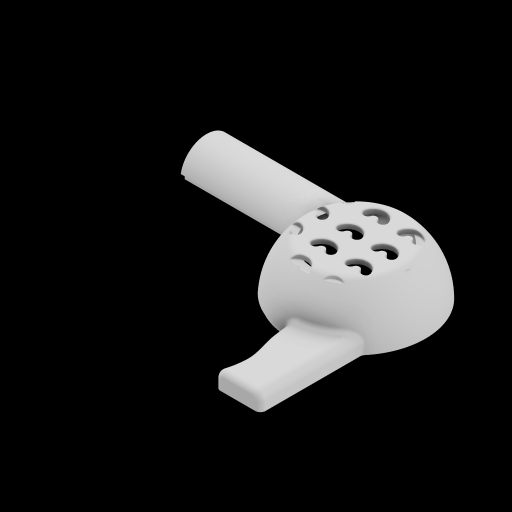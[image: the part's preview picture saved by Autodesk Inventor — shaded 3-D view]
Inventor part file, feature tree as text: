
AUTODESK INVENTOR PART (.ipt)
format: ipt  version: 2024 (Build 280153000, 153)  size: 583,680 bytes
history: native  units: in
note: dims shown in document units (in); Inventor stores cm internally (conversion verified against a paired STEP export)
features: sketch x9, plane x3, fillet x2, extrude x2, other x1, loft x1, shell x1, pattern_linear x1, sweep x1
ambient origin geometry x8: Origin, YZ Plane, XZ Plane, XY Plane, X Axis, Y Axis, Z Axis, Center Point
bodies: Solid1 (feature_tree)
feature tree (21):
  other  "BOWL SHAPE"
  fillet  "Fillet1"  Radius=4.0in
  plane  "Work Plane HANDLE1"
  plane  "Work Plane2 HANDLE2"
  plane  "Work Plane HANDLE 3"
  loft  "Loft1"
  extrude  "Extrusion1"  Depth=2.5in
  fillet  "Fillet2"  Radius=1.5in
  shell  "Shell1"  Thickness=0.5in
  extrude  "SINGLE VENT HOLE"  Depth=1.4in
  pattern_linear  "VENT PATTERN"  Spacing1=0.5in  [1 undecoded]
  sweep  "Sweep1"
  sketch  "Sketch1"  dims[d2=1.5in d3=90.0deg]
  sketch  "Sketch2"  dims[d4=0.25in d5=2.5in d6=3.5in d7=4.25in d8=1.5in d9=0.5in]
  sketch  "Sketch3"  dims[d10=0.25in d11=1.4in]
  sketch  "Sketch4"  dims[d12=0.5in]
  sketch  "Sketch5"  dims[d13=0.25in]
  sketch  "Sketch6"  dims[d14=1.2in]
  sketch  "Sketch7"  dims[d15=0.5in]
  sketch  "Sketch8"  dims[d16=0.25in]
  sketch  "Sketch9"  dims[d18=1.35in d19=0.5in d20=0.25in d21=0.0in d22=90.0deg d23=0.0in d24=90.0deg d25=0.0in d26=90.0deg d27=0.0in d28=90.0deg d29=0.75in d30=1.2in d31=5.5in d32=0.0in d33=0.15in d34=0.125in d35=0.125in d36=0.0in d37=4.3307in d39=1.0in d40=4.3307in d42=0.75in d45=0.1206in d46=0.3445in d50=3.4745in d51=3.0631in d52=0.0625in d53=0.125in d54=0.0in d55=0.0in]
note: 1 required parameter value undecoded (feature->parameter linkage not recoverable at this tier; creation-order binding heuristic only, values carry confidence <= 0.55)
